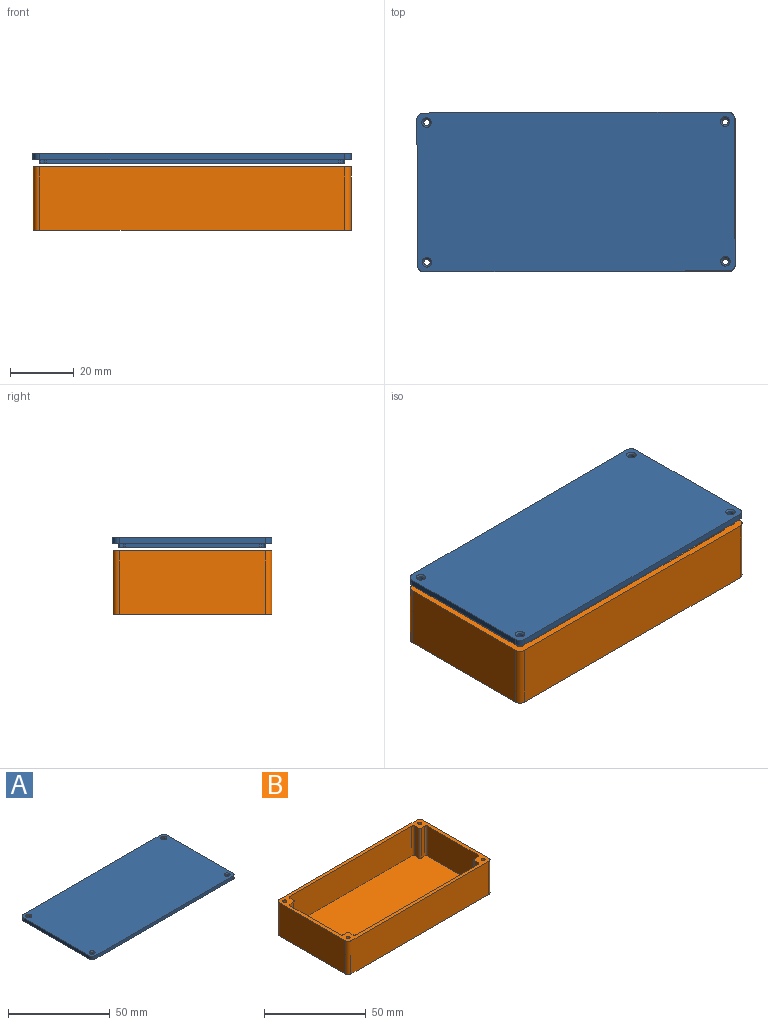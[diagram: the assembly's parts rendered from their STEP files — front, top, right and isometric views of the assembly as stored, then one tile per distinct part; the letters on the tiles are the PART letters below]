
ASSEMBLY  parts=2 mates=1
PART A: 31 faces, bbox 100x50x3 mm
  f0: cylinder r=2mm len=1mm, axis (0,0,1), area 0.6mm2, adj f13,f18,f22,f29
  f1: cylinder r=2mm len=1mm, axis (0,0,1), area 0.6mm2, adj f13,f19,f22,f29
  f2: cylinder r=2mm len=1mm, axis (0,0,-1), area 0.6mm2, adj f13,f20,f22,f27
  f3: cylinder r=2mm len=1mm, axis (0,0,-1), area 0.6mm2, adj f13,f19,f22,f27
  f4: cylinder r=2mm len=1mm, axis (0,0,1), area 0.6mm2, adj f13,f20,f22,f25
  f5: cylinder r=2mm len=1mm, axis (0,0,1), area 0.6mm2, adj f13,f21,f22,f25
  f6: cylinder r=2mm len=1mm, axis (0,0,-1), area 0.6mm2, adj f13,f18,f22,f23
  f7: cylinder r=2mm len=1mm, axis (0,0,-1), area 0.6mm2, adj f13,f21,f22,f23
  f8: plane 46x2mm, normal (-1,0,0), area 92mm2, adj f12,f13,f14,f17
  f9: plane 96x2mm, normal (0,-1,0), area 192mm2, adj f12,f13,f14,f15
  f10: plane 46x2mm, normal (1,0,0), area 92mm2, adj f12,f13,f15,f16
  f11: plane 96x2mm, normal (0,1,0), area 192mm2, adj f12,f13,f16,f17
  f12: plane 100x50mm, normal (0,0,1), area 4968.3mm2, adj f8,f9,f10,f11,f14,f15,f16,f17
  f13: plane 100x50mm, normal (0,0,-1), area 581.7mm2, adj f0,f1,f2,f3,f4,f5,f6,f7
  f14: cylinder r=2mm len=2mm, axis (0,0,1), area 6.3mm2, adj f8,f9,f12,f13
  f15: cylinder r=2mm len=2mm, axis (0,0,-1), area 6.3mm2, adj f9,f10,f12,f13
  f16: cylinder r=2mm len=2mm, axis (0,0,1), area 6.3mm2, adj f10,f11,f12,f13
  f17: cylinder r=2mm len=2mm, axis (0,0,-1), area 6.3mm2, adj f8,f11,f12,f13
  f18: plane 42x1mm, normal (1,0,0), area 42mm2, adj f0,f6,f13,f22
  f19: plane 92x1mm, normal (0,-1,0), area 92mm2, adj f1,f3,f13,f22
  f20: plane 42x1mm, normal (-1,0,0), area 42mm2, adj f2,f4,f13,f22
  f21: plane 92x1mm, normal (0,1,0), area 92mm2, adj f5,f7,f13,f22
  f22: plane 96x46mm, normal (0,0,-1), area 4402.3mm2, adj f0,f1,f2,f3,f4,f5,f6,f7
  f23: cylinder r=1mm len=2.5mm, axis (0,0,1), area 13.3mm2, adj f6,f7,f13,f22,f24
  f24: cone r=1mm half-angle=45deg, axis (0,0,1), area 5.6mm2, adj f12,f23
  f25: cylinder r=1mm len=2.5mm, axis (0,0,1), area 13.3mm2, adj f4,f5,f13,f22,f26
  f26: cone r=1mm half-angle=45deg, axis (0,0,1), area 5.6mm2, adj f12,f25
  f27: cylinder r=1mm len=2.5mm, axis (0,0,1), area 13.3mm2, adj f2,f3,f13,f22,f28
  f28: cone r=1mm half-angle=45deg, axis (0,0,1), area 5.6mm2, adj f12,f27
  f29: cylinder r=1mm len=2.5mm, axis (0,0,1), area 13.3mm2, adj f0,f1,f13,f22,f30
  f30: cone r=1mm half-angle=45deg, axis (0,0,1), area 5.6mm2, adj f12,f29
PART B: 39 faces, bbox 100x50x20 mm
  f0: plane 96x46mm, normal (0,0,1), area 4334.1mm2, adj f1,f2,f3,f4,f15,f16,f17,f18
  f1: plane 85x18mm, normal (0,1,0), area 1530mm2, adj f0,f5,f24,f29
  f2: plane 35x18mm, normal (-1,0,0), area 630mm2, adj f0,f5,f23,f26
  f3: plane 85x18mm, normal (0,-1,0), area 1530mm2, adj f0,f5,f25,f28
  f4: plane 35x18mm, normal (1,0,0), area 630mm2, adj f0,f5,f27,f30
  f5: plane 100x50mm, normal (0,0,1), area 649.9mm2, adj f1,f2,f3,f4,f6,f7,f8,f9
  f6: plane 96x20mm, normal (0,-1,0), area 1920mm2, adj f5,f10,f11,f14
  f7: plane 46x20mm, normal (1,0,0), area 920mm2, adj f5,f10,f11,f12
  f8: plane 96x20mm, normal (0,1,0), area 1920mm2, adj f5,f10,f12,f13
  f9: plane 46x20mm, normal (-1,0,0), area 920mm2, adj f5,f10,f13,f14
  f10: plane 100x50mm, normal (0,0,-1), area 4984mm2, adj f6,f7,f8,f9,f11,f12,f13,f14
  f11: cylinder r=2mm len=20mm, axis (0,0,1), area 62.8mm2, adj f5,f6,f7,f10
  f12: cylinder r=2mm len=20mm, axis (0,0,-1), area 62.8mm2, adj f5,f7,f8,f10
  f13: cylinder r=2mm len=20mm, axis (0,0,1), area 62.8mm2, adj f5,f8,f9,f10
  f14: cylinder r=2mm len=20mm, axis (0,0,-1), area 62.8mm2, adj f5,f6,f9,f10
  f15: plane 18x2.5mm, normal (1,0,0), area 45mm2, adj f0,f5,f29,f34
  f16: plane 18x2.5mm, normal (0,1,0), area 45mm2, adj f0,f5,f30,f34
  f17: plane 18x2.5mm, normal (0,-1,0), area 45mm2, adj f0,f5,f27,f33
  f18: plane 18x2.5mm, normal (1,0,0), area 45mm2, adj f0,f5,f28,f33
  f19: plane 18x2.5mm, normal (-1,0,0), area 45mm2, adj f0,f5,f25,f32
  f20: plane 18x2.5mm, normal (0,-1,0), area 45mm2, adj f0,f5,f26,f32
  f21: plane 18x2.5mm, normal (-1,0,0), area 45mm2, adj f0,f5,f24,f31
  f22: plane 18x2.5mm, normal (0,1,0), area 45mm2, adj f0,f5,f23,f31
  f23: cylinder r=1mm len=18mm, axis (0,0,1), area 28.3mm2, adj f0,f2,f5,f22
  f24: cylinder r=1mm len=18mm, axis (0,0,-1), area 28.3mm2, adj f0,f1,f5,f21
  f25: cylinder r=1mm len=18mm, axis (0,0,1), area 28.3mm2, adj f0,f3,f5,f19
  f26: cylinder r=1mm len=18mm, axis (0,0,-1), area 28.3mm2, adj f0,f2,f5,f20
  f27: cylinder r=1mm len=18mm, axis (0,0,1), area 28.3mm2, adj f0,f4,f5,f17
  f28: cylinder r=1mm len=18mm, axis (0,0,-1), area 28.3mm2, adj f0,f3,f5,f18
  f29: cylinder r=1mm len=18mm, axis (0,0,1), area 28.3mm2, adj f0,f1,f5,f15
  f30: cylinder r=1mm len=18mm, axis (0,0,-1), area 28.3mm2, adj f0,f4,f5,f16
  f31: cylinder r=1mm len=18mm, axis (0,0,1), area 28.3mm2, adj f0,f5,f21,f22
  f32: cylinder r=1mm len=18mm, axis (0,0,1), area 28.3mm2, adj f0,f5,f19,f20
  f33: cylinder r=1mm len=18mm, axis (0,0,1), area 28.3mm2, adj f0,f5,f17,f18
  f34: cylinder r=1mm len=18mm, axis (0,0,1), area 28.3mm2, adj f0,f5,f15,f16
  f35: cylinder r=1mm len=20mm, axis (0,0,1), area 125.7mm2, adj f5,f10
  f36: cylinder r=1mm len=20mm, axis (0,0,1), area 125.7mm2, adj f5,f10
  f37: cylinder r=1mm len=20mm, axis (0,0,1), area 125.7mm2, adj f5,f10
  f38: cylinder r=1mm len=20mm, axis (0,0,1), area 125.7mm2, adj f5,f10
PLACE A rot(axis=(0,0,1),0.2deg) t=(-229.96,-167.41,25.18)mm
PLACE B t=(-113.21,-51.57,2.97)mm fixed
MATE cylindrical A.f27 <-> B.f36  axis (0,0,1) through (-186.96,-148.75,25.43)mm
